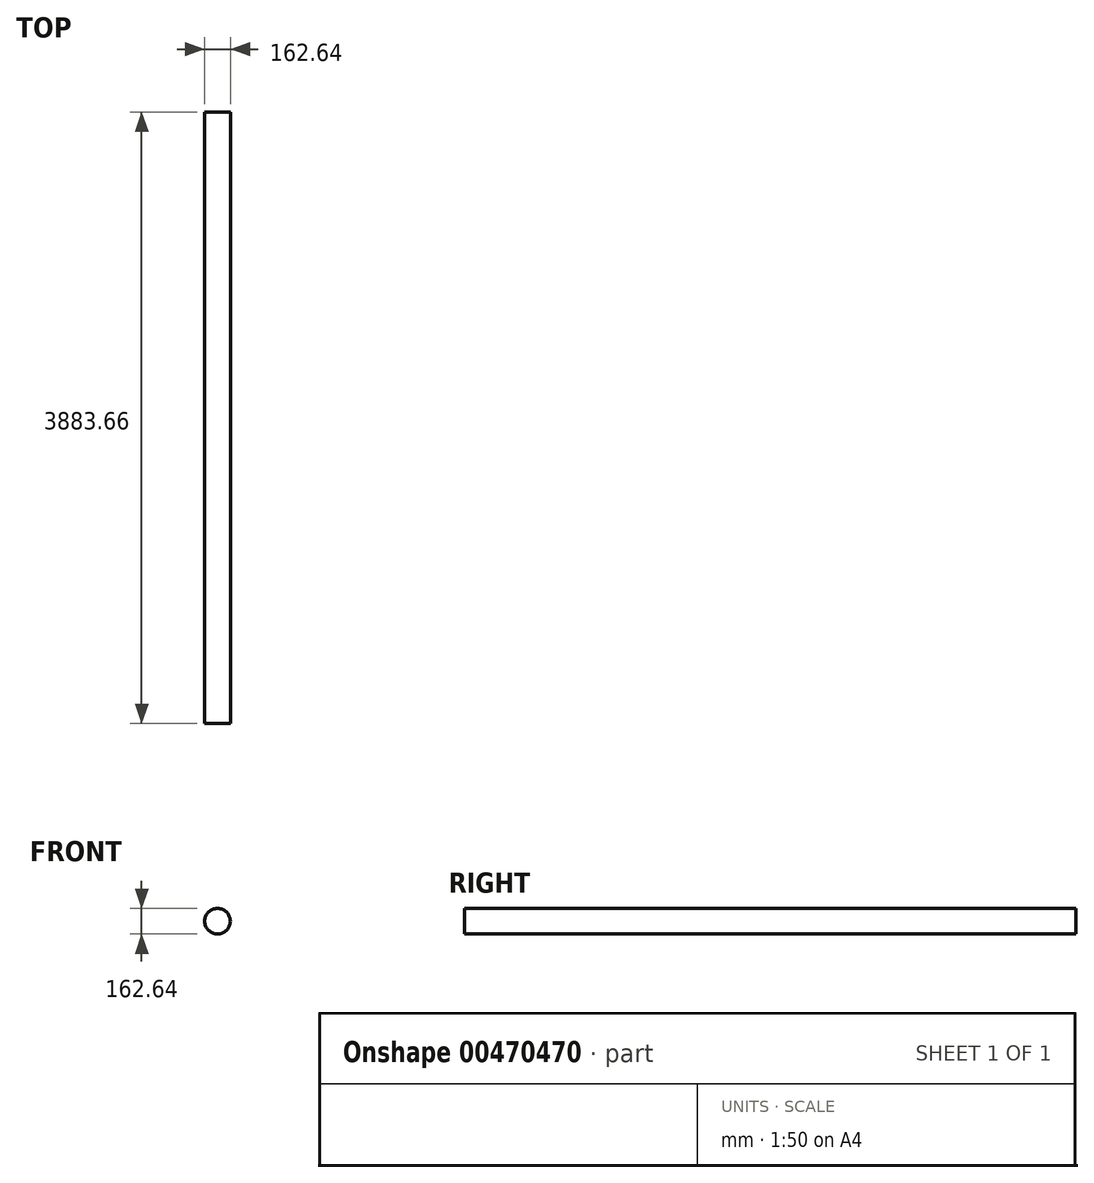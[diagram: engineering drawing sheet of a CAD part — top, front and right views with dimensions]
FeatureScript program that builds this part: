
annotation { "Feature Type Name" : "Feature", "Feature Type Description" : "" }
export const myFeature = defineFeature(function(context is Context, id is Id, definition is map)
    precondition{}
    {
        {
            var Q0;
            Q0=qCreatedBy(makeId("Front.planeOp"),FACE);
            var sketch = newSketch(context, id + "F0", { "sketchPlane" : qUnion([Q0])});
            skCircle(sketch, "E0", {"center": v(-68.34, 0) * mm, "radius": 81.32 * mm});
            skSolve(sketch);
        }
        {
            var Q0;
            Q0 = qSketchRegion(id + "F0", true);
            extrude(context, id + "F1", {"entities" : qUnion([Q0]), "depth" : 3883.66 * mm});
        }
    });
